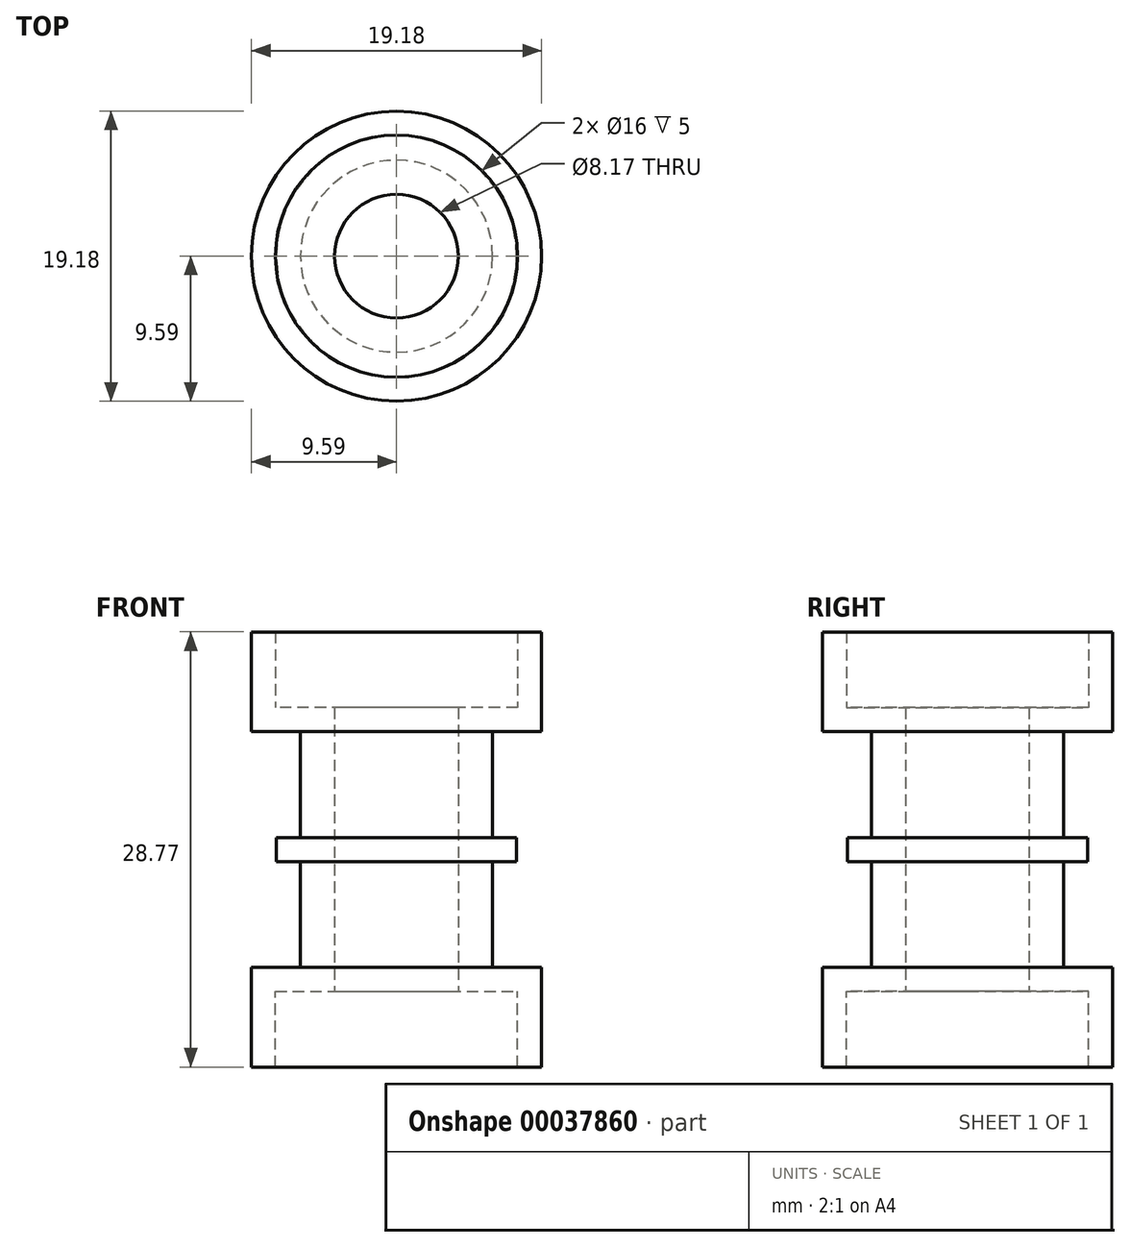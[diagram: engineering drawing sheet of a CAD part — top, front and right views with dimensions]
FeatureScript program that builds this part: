
annotation { "Feature Type Name" : "Feature", "Feature Type Description" : "" }
export const myFeature = defineFeature(function(context is Context, id is Id, definition is map)
    precondition{}
    {
        {
            var Q0;
            Q0=qCreatedBy(makeId("Top.planeOp"),FACE);
            var sketch = newSketch(context, id + "F0", { "sketchPlane" : qUnion([Q0])});
            skCircle(sketch, "E0", {"center": v(0, 0) * mm, "radius": 7.94 * mm});
            skSolve(sketch);
        }
        {
            var Q0;
            Q0 = qSketchRegion(id + "F0", true);
            extrude(context, id + "F1", {"entities" : qUnion([Q0]), "depth" : 1.59 * mm});
        }
        {
            var Q0;
            Q0=makeQuery(id+"F1.opExtrude","CAP_FACE",FACE,{"disambiguationData":[OSD([sQuery(id+"F0.wireOp",EDGE,"E0")])],"isStart":false});
            var sketch = newSketch(context, id + "F2", { "sketchPlane" : qUnion([Q0])});
            skCircle(sketch, "E1", {"center": v(0, 0) * mm, "radius": 6.35 * mm});
            skSolve(sketch);
        }
        {
            var Q0;
            Q0 = qSketchRegion(id + "F2", true);
            extrude(context, id + "F3", {"entities" : qUnion([Q0]), "operationType" : NewBodyOperationType.ADD, "depth" : 7 * mm});
        }
        {
            var Q0;
            Q0=makeQuery(id+"F1.opExtrude","CAP_FACE",FACE,{"disambiguationData":[OSD([sQuery(id+"F0.wireOp",EDGE,"E0")])],"isStart":true});
            var sketch = newSketch(context, id + "F4", { "sketchPlane" : qUnion([Q0])});
            skCircle(sketch, "E2", {"center": v(0, 0) * mm, "radius": 6.35 * mm});
            skSolve(sketch);
        }
        {
            var Q0;
            Q0 = qSketchRegion(id + "F4", true);
            extrude(context, id + "F5", {"entities" : qUnion([Q0]), "operationType" : NewBodyOperationType.ADD, "depth" : 7 * mm});
        }
        {
            var Q0;
            Q0=makeQuery(id+"F3.opExtrude","CAP_FACE",FACE,{"disambiguationData":[OSD([sQuery(id+"F2.wireOp",EDGE,"E1")])],"isStart":false});
            var sketch = newSketch(context, id + "F6", { "sketchPlane" : qUnion([Q0])});
            skCircle(sketch, "E3", {"center": v(0, 0) * mm, "radius": 9.59 * mm});
            skSolve(sketch);
        }
        {
            var Q0;
            Q0 = qSketchRegion(id + "F6", true);
            extrude(context, id + "F7", {"entities" : qUnion([Q0]), "operationType" : NewBodyOperationType.ADD, "depth" : 1.59 * mm});
        }
        {
            var Q0;
            Q0=makeQuery(id+"F5.opExtrude","CAP_FACE",FACE,{"disambiguationData":[OSD([sQuery(id+"F4.wireOp",EDGE,"E2")])],"isStart":false});
            var sketch = newSketch(context, id + "F8", { "sketchPlane" : qUnion([Q0])});
            skCircle(sketch, "E4", {"center": v(0, 0) * mm, "radius": 9.59 * mm});
            skSolve(sketch);
        }
        {
            var Q0;
            Q0 = qSketchRegion(id + "F8", true);
            extrude(context, id + "F9", {"entities" : qUnion([Q0]), "operationType" : NewBodyOperationType.ADD, "depth" : 1.59 * mm});
        }
        {
            var Q0;
            Q0=makeQuery(id+"F7.opExtrude","CAP_FACE",FACE,{"disambiguationData":[OSD([sQuery(id+"F6.wireOp",EDGE,"E3")])],"isStart":false});
            var sketch = newSketch(context, id + "F10", { "sketchPlane" : qUnion([Q0])});
            skCircle(sketch, "E5", {"center": v(0, 0) * mm, "radius": 9.59 * mm});
            skCircle(sketch, "E6", {"center": v(0, 0) * mm, "radius": 8 * mm});
            skSolve(sketch);
        }
        {
            var Q0;
            Q0 = qSketchRegion(id + "F10", true);
            extrude(context, id + "F11", {"entities" : qUnion([Q0]), "operationType" : NewBodyOperationType.ADD, "depth" : 5 * mm});
        }
        {
            var Q0;
            Q0=makeQuery(id+"F9.opExtrude","CAP_FACE",FACE,{"disambiguationData":[OSD([sQuery(id+"F8.wireOp",EDGE,"E4")])],"isStart":false});
            var sketch = newSketch(context, id + "F12", { "sketchPlane" : qUnion([Q0])});
            skCircle(sketch, "E7", {"center": v(0, 0) * mm, "radius": 9.59 * mm});
            skCircle(sketch, "E8", {"center": v(0, 0) * mm, "radius": 8 * mm});
            skSolve(sketch);
        }
        {
            var Q0;
            Q0 = qSketchRegion(id + "F12", true);
            extrude(context, id + "F13", {"entities" : qUnion([Q0]), "operationType" : NewBodyOperationType.ADD, "depth" : 5 * mm});
        }
        {
            var Q0;
            Q0=makeQuery(id+"F9.opExtrude","CAP_FACE",FACE,{"disambiguationData":[OSD([sQuery(id+"F8.wireOp",EDGE,"E4")])],"isStart":false});
            var sketch = newSketch(context, id + "F14", { "sketchPlane" : qUnion([Q0])});
            skCircle(sketch, "E9", {"center": v(0, 0) * mm, "radius": 4.09 * mm});
            skSolve(sketch);
        }
        {
            var Q0;
            Q0 = qSketchRegion(id + "F14", true);
            var Q1;
            Q1=makeQuery(id+"F7.opExtrude","CAP_FACE",FACE,{"disambiguationData":[OSD([sQuery(id+"F6.wireOp",EDGE,"E3")])],"isStart":false});
            extrude(context, id + "F15", {"entities" : qUnion([Q0]), "operationType" : NewBodyOperationType.REMOVE, "endBound" : BoundingType.UP_TO_SURFACE, "oppositeDirection" : true, "endBoundEntityFace" : qUnion([Q1]), "depth" : 25.4 * mm});
        }
    });
